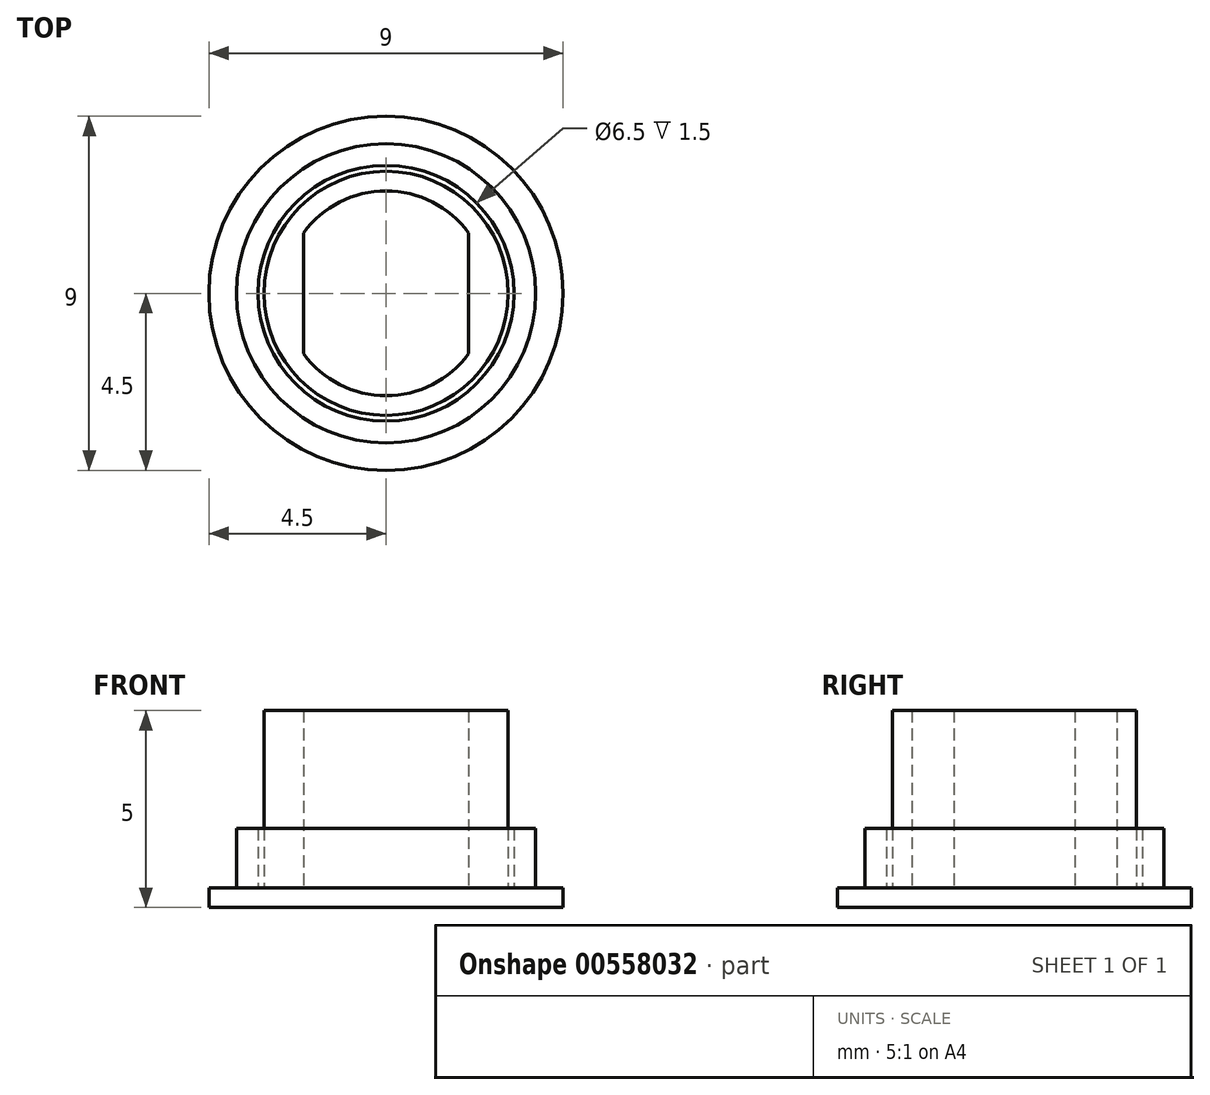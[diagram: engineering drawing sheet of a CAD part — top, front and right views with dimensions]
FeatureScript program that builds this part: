
annotation { "Feature Type Name" : "Feature", "Feature Type Description" : "" }
export const myFeature = defineFeature(function(context is Context, id is Id, definition is map)
    precondition{}
    {
        {
            var Q0;
            Q0=qCreatedBy(makeId("Top.planeOp"),FACE);
            var sketch = newSketch(context, id + "F0", { "sketchPlane" : qUnion([Q0])});
            skCircle(sketch, "E0", {"center": v(0, 0) * mm, "radius": 4.5 * mm});
            skCircle(sketch, "E1", {"center": v(0, 0) * mm, "radius": 3.8 * mm});
            skCircle(sketch, "E2", {"center": v(0, 0) * mm, "radius": 3.25 * mm});
            skSolve(sketch);
        }
        {
            var Q0;
            Q0=makeQuery(id+"F0.imprint","IMPRINT",FACE,{"disambiguationData":[TD([[makeQuery(id+"F0.imprint","IMPRINT",EDGE,{"derivedFrom":sQuery(id+"F0.wireOp",EDGE,"E0")}),1.0]])]});
            var Q1;
            Q1=makeQuery(id+"F0.imprint","IMPRINT",FACE,{"disambiguationData":[TD([[makeQuery(id+"F0.imprint","IMPRINT",EDGE,{"derivedFrom":sQuery(id+"F0.wireOp",EDGE,"E1")}),1.0]])]});
            extrude(context, id + "F1", {"entities" : qUnion([Q0, Q1]), "depth" : .5 * mm, "offsetDistance" : 25 * mm});
        }
        {
            var Q0;
            Q0=makeQuery(id+"F0.imprint","IMPRINT",FACE,{"disambiguationData":[TD([[makeQuery(id+"F0.imprint","IMPRINT",EDGE,{"derivedFrom":sQuery(id+"F0.wireOp",EDGE,"E1")}),1.0]])]});
            extrude(context, id + "F2", {"entities" : qUnion([Q0]), "operationType" : NewBodyOperationType.ADD, "depth" : 2 * mm, "offsetDistance" : 25 * mm});
        }
        {
            var Q0;
            Q0=makeQuery(id+"F0.imprint","IMPRINT",FACE,{"disambiguationData":[TD([[makeQuery(id+"F0.imprint","IMPRINT",EDGE,{"derivedFrom":sQuery(id+"F0.wireOp",EDGE,"E2")}),1.0]])]});
            var sketch = newSketch(context, id + "F3", { "sketchPlane" : qUnion([Q0])});
            skCircle(sketch, "E3", {"center": v(0, 0) * mm, "radius": 2.6 * mm});
            skCircle(sketch, "E4", {"center": v(0, 0) * mm, "radius": 3.1 * mm});
            skLineSegment(sketch, "E5", {"start": v(-2.1, -1.53) * mm, "end": v(-2.1, 1.53) * mm});
            skLineSegment(sketch, "E6", {"start": v(2.1, -1.53) * mm, "end": v(2.1, 1.53) * mm});
            skSolve(sketch);
        }
        {
            var Q0;
            {var subQ0=sQuery(id+"F3.wireOp",EDGE,"E6");Q0=makeQuery(id+"F3.imprint","IMPRINT",FACE,{"disambiguationData":[TD([[makeQuery(id+"F3.imprint","IMPRINT",EDGE,{"derivedFrom":subQ0}),-1.0]])]});}
            var Q1;
            {var subQ0=sQuery(id+"F3.wireOp",EDGE,"E5");Q1=makeQuery(id+"F3.imprint","IMPRINT",FACE,{"disambiguationData":[TD([[makeQuery(id+"F3.imprint","IMPRINT",EDGE,{"derivedFrom":subQ0}),1.0]])]});}
            var Q2;
            Q2=makeQuery(id+"F3.imprint","IMPRINT",FACE,{"disambiguationData":[TD([[makeQuery(id+"F3.imprint","IMPRINT",EDGE,{"derivedFrom":sQuery(id+"F3.wireOp",EDGE,"E4")}),1.0]])]});
            extrude(context, id + "F4", {"entities" : qUnion([Q0, Q1, Q2]), "depth" : 5 * mm, "offsetDistance" : 25 * mm});
        }
        {
            var Q0;
            Q0=makeQuery(id+"F0.imprint","IMPRINT",FACE,{"disambiguationData":[TD([[makeQuery(id+"F0.imprint","IMPRINT",EDGE,{"derivedFrom":sQuery(id+"F0.wireOp",EDGE,"E2")}),1.0]])]});
            extrude(context, id + "F5", {"entities" : qUnion([Q0]), "operationType" : NewBodyOperationType.ADD, "depth" : .5 * mm, "offsetDistance" : 25 * mm});
        }
    });
